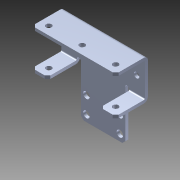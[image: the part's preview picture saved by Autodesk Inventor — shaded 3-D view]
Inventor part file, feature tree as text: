
AUTODESK INVENTOR PART (.ipt)
format: ipt  version: 2014 (Build 180170000, 170)  size: 173,056 bytes
history: native  units: in
note: dims shown in document units (in); Inventor stores cm internally (conversion verified against a paired STEP export)
features: chamfer x1, other x1, imported_body x1
ambient origin geometry x8: Origin, YZ Plane, XZ Plane, XY Plane, X Axis, Y Axis, Z Axis, Center Point
bodies: Body1 (feature_tree)
feature tree (3):
  chamfer  "Chamfer1"  [1 undecoded]
  other  "217-3558-STEP1"
  imported_body  "Base1"
note: 1 required parameter value undecoded (feature->parameter linkage not recoverable at this tier; creation-order binding heuristic only, values carry confidence <= 0.55)
